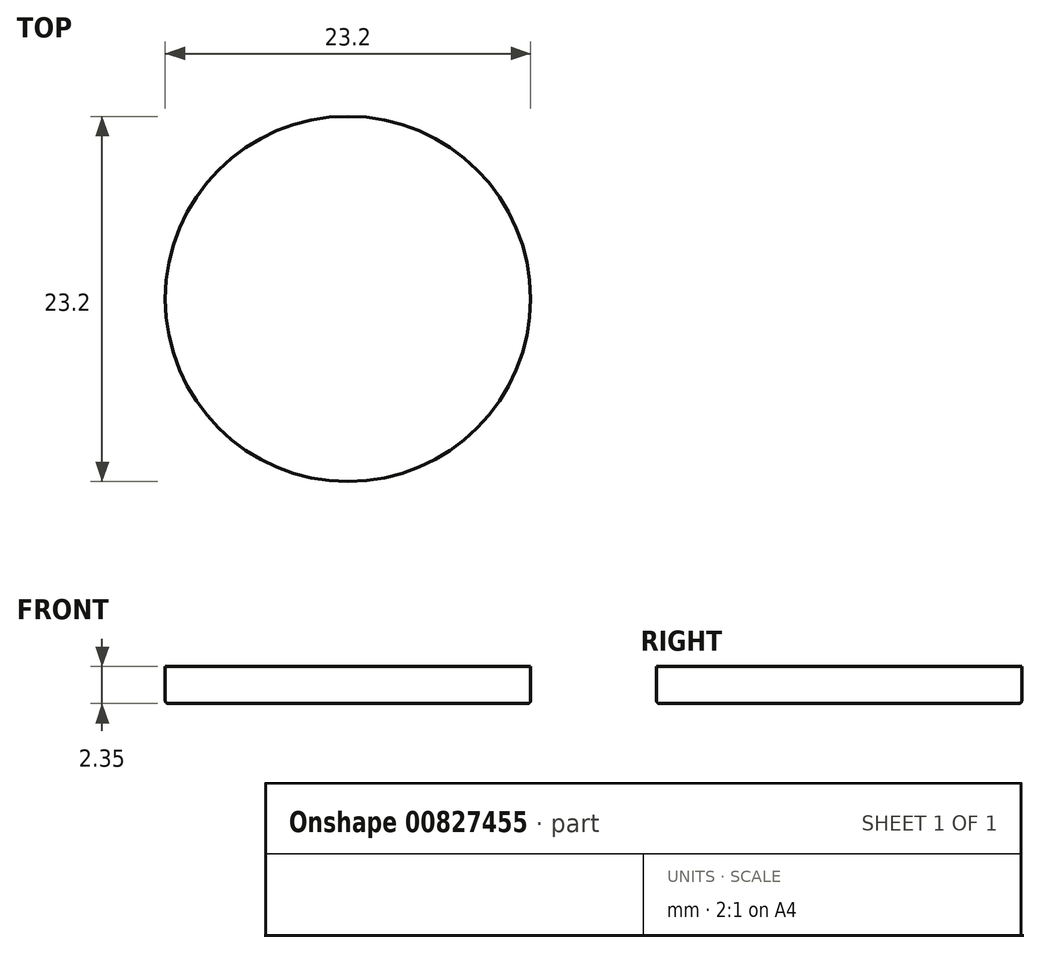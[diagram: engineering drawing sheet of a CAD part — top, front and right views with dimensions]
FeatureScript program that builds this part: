
annotation { "Feature Type Name" : "Feature", "Feature Type Description" : "" }
export const myFeature = defineFeature(function(context is Context, id is Id, definition is map)
    precondition{}
    {
        {
            var Q0;
            Q0=qCreatedBy(makeId("Top.planeOp"),FACE);
            var sketch = newSketch(context, id + "F0", { "sketchPlane" : qUnion([Q0])});
            skCircle(sketch, "E0", {"center": v(0, 0) * mm, "radius": 11.6 * mm});
            skSolve(sketch);
        }
        {
            var Q0;
            Q0 = qSketchRegion(id + "F0", true);
            extrude(context, id + "F1", {"entities" : qUnion([Q0]), "depth" : 2.15 * mm, "offsetDistance" : 25 * mm});
        }
        {
            var Q0;
            Q0=makeQuery(id+"F1.opExtrude","CAP_FACE",FACE,{"disambiguationData":[OSD([sQuery(id+"F0.wireOp",EDGE,"E0")])],"isStart":false});
            var sketch = newSketch(context, id + "F2", { "sketchPlane" : qUnion([Q0])});
            skText(sketch, "E1", { "text": "1CHF", "fontName": "OpenSans-BoldItalic.ttf"});
            const initialGuessF2  = {"E1": [-0.00727, -0.00183, 1, 0, 0.00432]};
            skSetInitialGuess(sketch, initialGuessF2);
            skSolve(sketch);
        }
        {
            var Q0;
            Q0 = qSketchRegion(id + "F2", true);
            var Q1;
            Q1=makeQuery(id+"F2.imprint","IMPRINT",FACE,{"disambiguationData":[TD([[makeQuery(id+"F2.imprint","IMPRINT",EDGE,{"derivedFrom":sQuery(id+"F2.wireOp",EDGE,"E1.sketch_text.stroke-0")}),1.0]])]});
            var Q2;
            Q2=makeQuery(id+"F1.opExtrude","CAP_FACE",FACE,{"disambiguationData":[OSD([sQuery(id+"F0.wireOp",EDGE,"E0")])],"isStart":true});
            extrude(context, id + "F3", {"entities" : qUnion([Q0, Q1, Q2]), "operationType" : NewBodyOperationType.ADD, "depth" : 0.2 * mm, "offsetDistance" : 25 * mm});
        }
        {
            var Q0;
            Q0=makeQuery(id+"F1.opExtrude","CAP_EDGE",EDGE,{"disambiguationData":[OSD([sQuery(id+"F0.wireOp",EDGE,"E0")])],"isStart":true});
            var Q1;
            Q1=makeQuery(id+"F1.opExtrude","CAP_EDGE",EDGE,{"disambiguationData":[OSD([sQuery(id+"F0.wireOp",EDGE,"E0")])],"isStart":false});
            fillet(context, id + "F4", {"entities" : qUnion([Q0, Q1]), "radius" : 0.2 * mm, "tangentPropagation" : true, "allowEdgeOverflow" : false});
        }
    });
